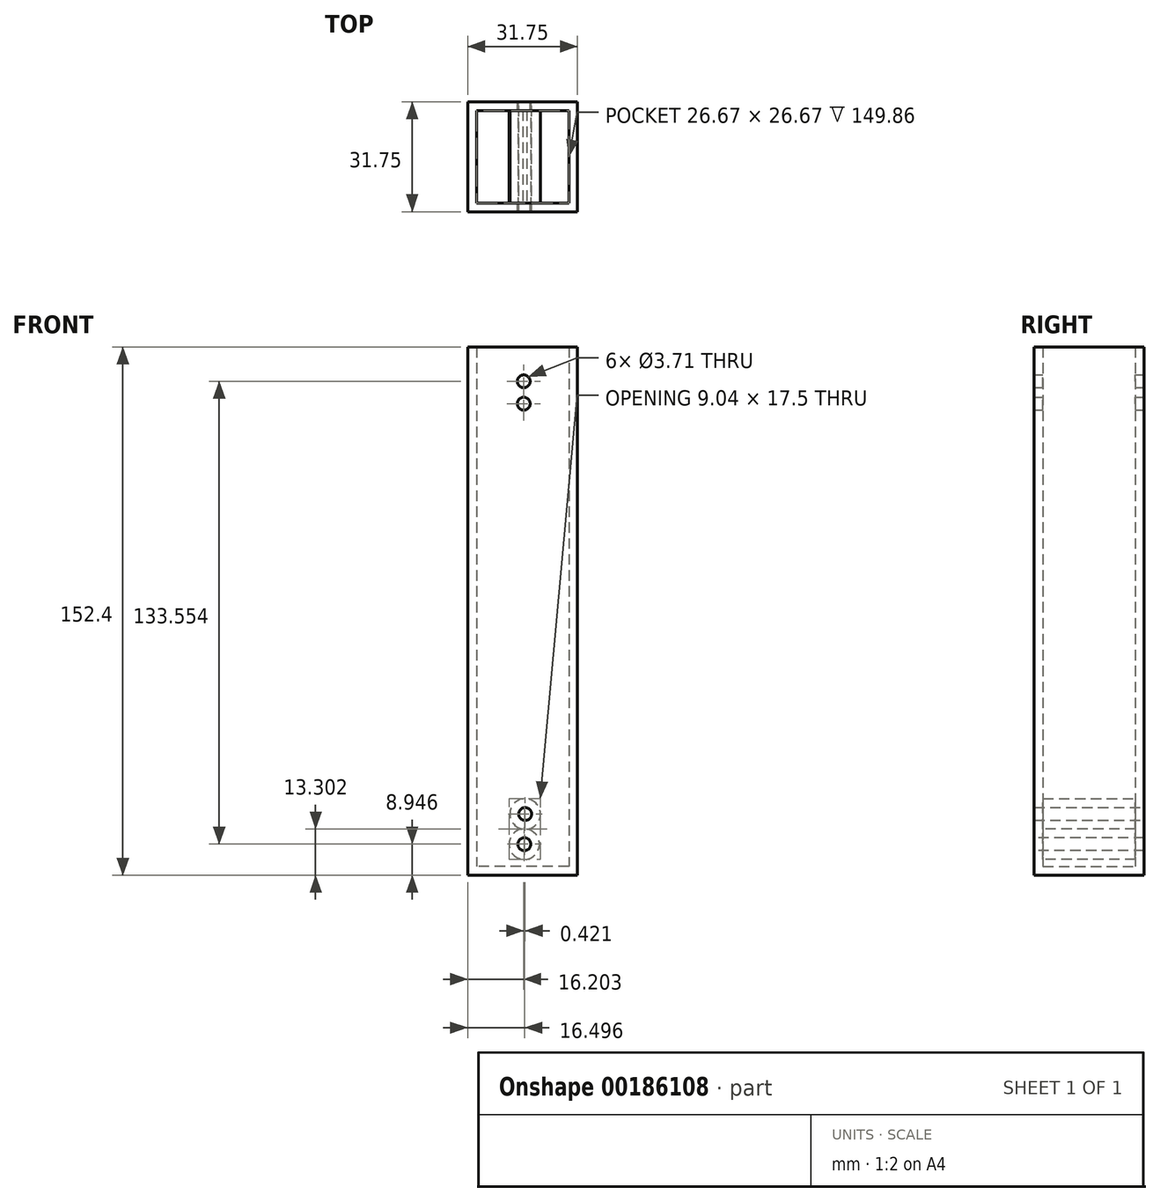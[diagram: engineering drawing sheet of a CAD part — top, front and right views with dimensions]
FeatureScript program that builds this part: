
annotation { "Feature Type Name" : "Feature", "Feature Type Description" : "" }
export const myFeature = defineFeature(function(context is Context, id is Id, definition is map)
    precondition{}
    {
        {
            var Q0;
            Q0=qCreatedBy(makeId("Top.planeOp"),FACE);
            var sketch = newSketch(context, id + "F0", { "sketchPlane" : qUnion([Q0])});
            skLineSegment(sketch, "E0.bottom", {"start": v(-12.07, -42.66) * mm, "end": v(-43.82, -42.66) * mm});
            skLineSegment(sketch, "E0.top", {"start": v(-12.07, -10.91) * mm, "end": v(-43.82, -10.91) * mm});
            skLineSegment(sketch, "E0.left", {"start": v(-12.07, -42.66) * mm, "end": v(-12.07, -10.91) * mm});
            skLineSegment(sketch, "E0.right", {"start": v(-43.82, -42.66) * mm, "end": v(-43.82, -10.91) * mm});
            skSolve(sketch);
        }
        {
            var Q0;
            Q0=makeQuery(id+"F0.imprint","IMPRINT",FACE,{"disambiguationData":[TD([[makeQuery(id+"F0.imprint","IMPRINT",EDGE,{"derivedFrom":sQuery(id+"F0.wireOp",EDGE,"E0.bottom")}),-1.0]])]});
            extrude(context, id + "F1", {"entities" : qUnion([Q0]), "depth" : 152.4 * mm});
        }
        {
            var Q0;
            Q0=makeQuery(id+"F1.opExtrude","SWEPT_FACE",FACE,{"disambiguationData":[OSD([sQuery(id+"F0.wireOp",EDGE,"E0.bottom")])]});
            var sketch = newSketch(context, id + "F2", { "sketchPlane" : qUnion([Q0])});
            skCircle(sketch, "E1", {"center": v(-27.45, 8.95) * mm, "radius": 1.85 * mm});
            skSolve(sketch);
        }
        {
            var Q0;
            Q0=sQuery(id+"F2.wireOp",VERTEX,"E1.center");
            var Q1;
            Q1=makeQuery(id+"F1.opExtrude","SWEPT_BODY",BODY,{"disambiguationData":[OSD([sQuery(id+"F0.wireOp",EDGE,"E0.bottom"),sQuery(id+"F0.wireOp",EDGE,"E0.top"),sQuery(id+"F0.wireOp",EDGE,"E0.left"),sQuery(id+"F0.wireOp",EDGE,"E0.right")])]});
            hole(context, id + "F3", {"style" : HoleStyle.SIMPLE, "endStyle" : HoleEndStyle.THROUGH, "holeDiameter" : 3.7 * mm, "locations" : qUnion([Q0]), "scope" : qUnion([Q1]), "isTappedThrough" : true});
        }
        {
            var Q0;
            Q0=makeQuery(id+"F1.opExtrude","SWEPT_FACE",FACE,{"disambiguationData":[OSD([sQuery(id+"F0.wireOp",EDGE,"E0.top")])]});
            var sketch = newSketch(context, id + "F4", { "sketchPlane" : qUnion([Q0])});
            skCircle(sketch, "E2", {"center": v(27.2, 17.66) * mm, "radius": 1.85 * mm});
            skSolve(sketch);
        }
        {
            var Q0;
            Q0=sQuery(id+"F4.wireOp",VERTEX,"E2.center");
            var Q1;
            Q1=makeQuery(id+"F1.opExtrude","SWEPT_BODY",BODY,{"disambiguationData":[OSD([sQuery(id+"F0.wireOp",EDGE,"E0.bottom"),sQuery(id+"F0.wireOp",EDGE,"E0.top"),sQuery(id+"F0.wireOp",EDGE,"E0.left"),sQuery(id+"F0.wireOp",EDGE,"E0.right")])]});
            hole(context, id + "F5", {"style" : HoleStyle.SIMPLE, "endStyle" : HoleEndStyle.THROUGH, "holeDiameter" : 3.7 * mm, "locations" : qUnion([Q0]), "scope" : qUnion([Q1]), "isTappedThrough" : true});
        }
        {
            var Q0;
            Q0=makeQuery(id+"F1.opExtrude","CAP_FACE",FACE,{"disambiguationData":[OSD([sQuery(id+"F0.wireOp",EDGE,"E0.bottom"),sQuery(id+"F0.wireOp",EDGE,"E0.top"),sQuery(id+"F0.wireOp",EDGE,"E0.left"),sQuery(id+"F0.wireOp",EDGE,"E0.right")])],"isStart":false});
            shell(context, id + "F6", {"entities" : qUnion([Q0]), "thickness" : 2.54 * mm});
        }
        {
            var Q0;
            Q0=makeQuery(id+"F1.opExtrude","SWEPT_FACE",FACE,{"disambiguationData":[OSD([sQuery(id+"F0.wireOp",EDGE,"E0.top")])]});
            var sketch = newSketch(context, id + "F7", { "sketchPlane" : qUnion([Q0])});
            skCircle(sketch, "E3", {"center": v(27.62, 142.5) * mm, "radius": 1.85 * mm});
            skSolve(sketch);
        }
        {
            var Q0;
            Q0=makeQuery(id+"F7.imprint","IMPRINT",FACE,{"disambiguationData":[TD([[makeQuery(id+"F7.imprint","IMPRINT",EDGE,{"derivedFrom":sQuery(id+"F7.wireOp",EDGE,"E3")}),-1.0]])]});
            var sketch = newSketch(context, id + "F8", { "sketchPlane" : qUnion([Q0])});
            skCircle(sketch, "E4", {"center": v(27.62, 136.04) * mm, "radius": 1.85 * mm});
            skSolve(sketch);
        }
        {
            var Q0;
            Q0=sQuery(id+"F7.wireOp",VERTEX,"E3.center");
            var Q1;
            Q1=sQuery(id+"F8.wireOp",VERTEX,"E4.center");
            var Q2;
            Q2=makeQuery(id+"F1.opExtrude","SWEPT_BODY",BODY,{"disambiguationData":[OSD([sQuery(id+"F0.wireOp",EDGE,"E0.bottom"),sQuery(id+"F0.wireOp",EDGE,"E0.top"),sQuery(id+"F0.wireOp",EDGE,"E0.left"),sQuery(id+"F0.wireOp",EDGE,"E0.right")])]});
            hole(context, id + "F9", {"style" : HoleStyle.SIMPLE, "endStyle" : HoleEndStyle.THROUGH, "holeDiameter" : 3.7 * mm, "locations" : qUnion([Q0, Q1]), "scope" : qUnion([Q2]), "isTappedThrough" : true});
        }
    });
